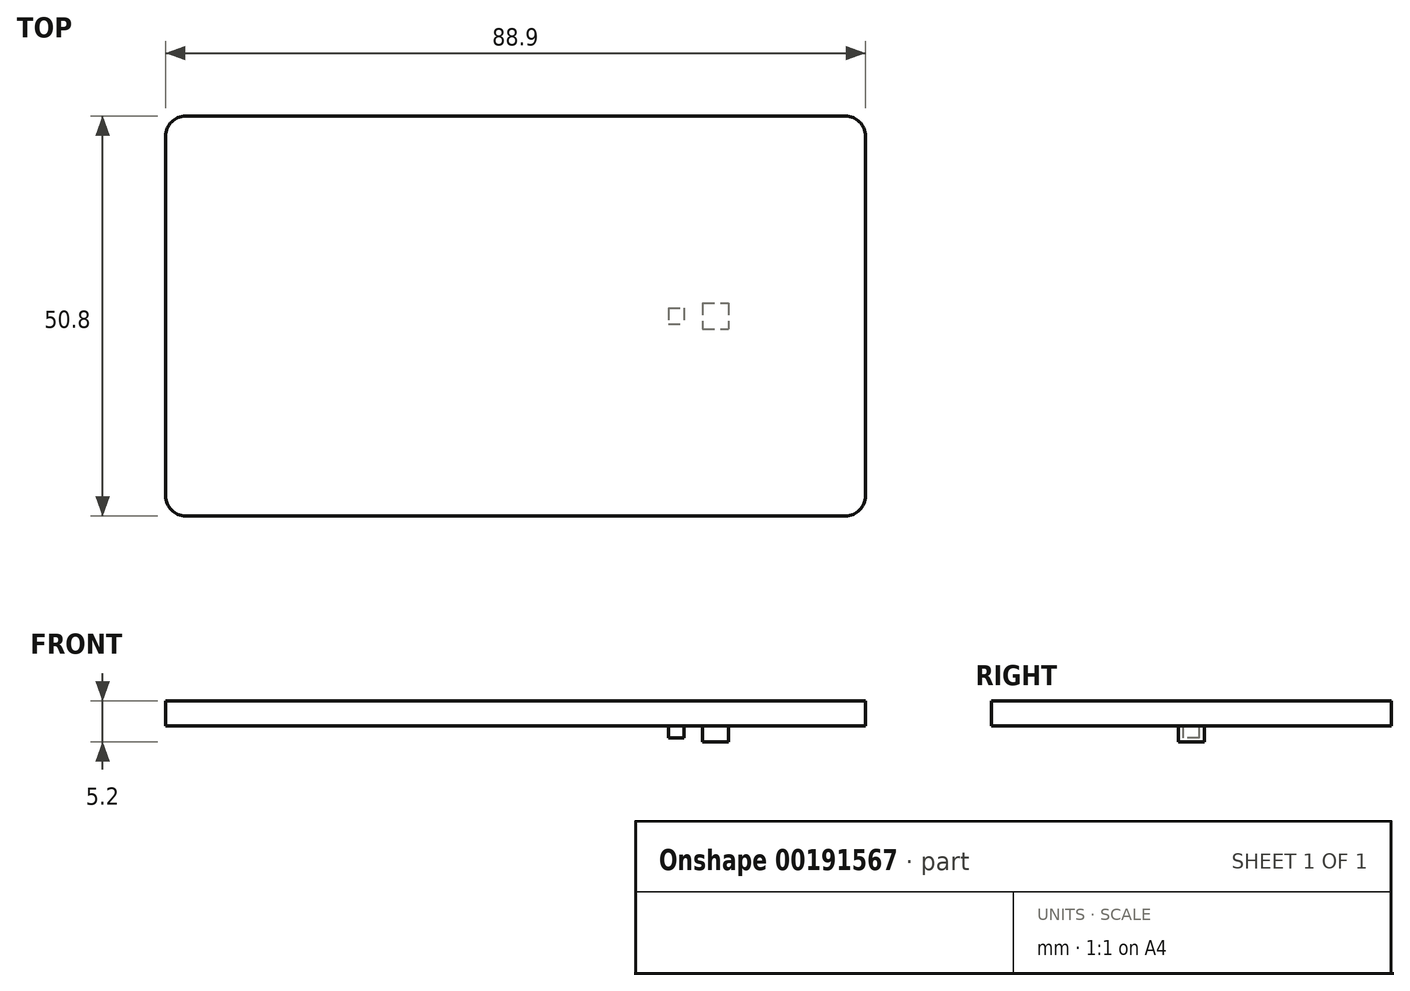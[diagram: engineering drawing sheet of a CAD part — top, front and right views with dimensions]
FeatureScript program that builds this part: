
annotation { "Feature Type Name" : "Feature", "Feature Type Description" : "" }
export const myFeature = defineFeature(function(context is Context, id is Id, definition is map)
    precondition{}
    {
        {
            var Q0;
            Q0=qCreatedBy(makeId("Top.planeOp"),FACE);
            var sketch = newSketch(context, id + "F0", { "sketchPlane" : qUnion([Q0])});
            skLineSegment(sketch, "E0.bottom", {"start": v(44.45, 25.4) * mm, "end": v(-44.45, 25.4) * mm});
            skLineSegment(sketch, "E0.top", {"start": v(44.45, -25.4) * mm, "end": v(-44.45, -25.4) * mm});
            skLineSegment(sketch, "E0.left", {"start": v(44.45, 25.4) * mm, "end": v(44.45, -25.4) * mm});
            skLineSegment(sketch, "E0.right", {"start": v(-44.45, 25.4) * mm, "end": v(-44.45, -25.4) * mm});
            skPoint(sketch, "E0.middle", {"position": v(0, 0) * mm});
            skSolve(sketch);
        }
        {
            var Q0;
            Q0 = qSketchRegion(id + "F0", true);
            extrude(context, id + "F1", {"entities" : qUnion([Q0]), "depth" : 3.2 * mm});
        }
        {
            var Q0;
            Q0=makeQuery(id+"F1.opExtrude","SWEPT_EDGE",EDGE,{"disambiguationData":[OSD([sQuery(id+"F0.wireOp",EDGE,"E0.top"),sQuery(id+"F0.wireOp",EDGE,"E0.left")])]});
            var Q1;
            Q1=makeQuery(id+"F1.opExtrude","SWEPT_EDGE",EDGE,{"disambiguationData":[OSD([sQuery(id+"F0.wireOp",EDGE,"E0.bottom"),sQuery(id+"F0.wireOp",EDGE,"E0.left")])]});
            var Q2;
            Q2=makeQuery(id+"F1.opExtrude","SWEPT_EDGE",EDGE,{"disambiguationData":[OSD([sQuery(id+"F0.wireOp",EDGE,"E0.top"),sQuery(id+"F0.wireOp",EDGE,"E0.right")])]});
            var Q3;
            Q3=makeQuery(id+"F1.opExtrude","SWEPT_EDGE",EDGE,{"disambiguationData":[OSD([sQuery(id+"F0.wireOp",EDGE,"E0.bottom"),sQuery(id+"F0.wireOp",EDGE,"E0.right")])]});
            fillet(context, id + "F2", {"entities" : qUnion([Q0, Q1, Q2, Q3]), "radius" : 2.54 * mm, "tangentPropagation" : true, "allowEdgeOverflow" : false});
        }
        {
            var Q0;
            Q0=makeQuery(id+"F1.opExtrude","CAP_FACE",FACE,{"disambiguationData":[OSD([sQuery(id+"F0.wireOp",EDGE,"E0.bottom"),sQuery(id+"F0.wireOp",EDGE,"E0.top"),sQuery(id+"F0.wireOp",EDGE,"E0.left"),sQuery(id+"F0.wireOp",EDGE,"E0.right")])],"isStart":true});
            var sketch = newSketch(context, id + "F3", { "sketchPlane" : qUnion([Q0])});
            skPoint(sketch, "E1", {"position": v(25.4, 0) * mm});
            skSolve(sketch);
        }
        {
            var Q0;
            {var subQ3=sQuery(id+"F0.wireOp",EDGE,"E0.bottom");Q0=makeQuery(id+"F3.imprint","IMPRINT",FACE,{"disambiguationData":[TD([[makeQuery(id+"F3.imprint","IMPRINT",EDGE,{"derivedFrom":makeQuery(id+"F1.opExtrude","CAP_EDGE",EDGE,{"disambiguationData":[OSD([subQ3])],"isStart":true})}),-1.0]])]});}
            var sketch = newSketch(context, id + "F4", { "sketchPlane" : qUnion([Q0])});
            skLineSegment(sketch, "E2.bottom", {"start": v(23.75, -1.65) * mm, "end": v(27.05, -1.65) * mm});
            skLineSegment(sketch, "E2.top", {"start": v(23.75, 1.65) * mm, "end": v(27.05, 1.65) * mm});
            skLineSegment(sketch, "E2.left", {"start": v(23.75, -1.65) * mm, "end": v(23.75, 1.65) * mm});
            skLineSegment(sketch, "E2.right", {"start": v(27.05, -1.65) * mm, "end": v(27.05, 1.65) * mm});
            skPoint(sketch, "E2.middle", {"position": v(25.4, 0) * mm});
            skSolve(sketch);
        }
        {
            var Q0;
            Q0 = qSketchRegion(id + "F4", true);
            extrude(context, id + "F5", {"entities" : qUnion([Q0]), "operationType" : NewBodyOperationType.ADD, "depth" : 2 * mm});
        }
        {
            var Q0;
            {var subQ3=sQuery(id+"F0.wireOp",EDGE,"E0.bottom");Q0=makeQuery(id+"F3.imprint","IMPRINT",FACE,{"disambiguationData":[TD([[makeQuery(id+"F3.imprint","IMPRINT",EDGE,{"derivedFrom":makeQuery(id+"F1.opExtrude","CAP_EDGE",EDGE,{"disambiguationData":[OSD([subQ3])],"isStart":true})}),-1.0]])]});}
            var sketch = newSketch(context, id + "F6", { "sketchPlane" : qUnion([Q0])});
            skPoint(sketch, "E3", {"position": v(20.4, 0) * mm});
            skSolve(sketch);
        }
        {
            var Q0;
            {var subQ3=sQuery(id+"F0.wireOp",EDGE,"E0.bottom");Q0=makeQuery(id+"F3.imprint","IMPRINT",FACE,{"disambiguationData":[TD([[makeQuery(id+"F3.imprint","IMPRINT",EDGE,{"derivedFrom":makeQuery(id+"F1.opExtrude","CAP_EDGE",EDGE,{"disambiguationData":[OSD([subQ3])],"isStart":true})}),-1.0]])]});}
            var sketch = newSketch(context, id + "F7", { "sketchPlane" : qUnion([Q0])});
            skLineSegment(sketch, "E4.bottom", {"start": v(19.4, -1) * mm, "end": v(21.4, -1) * mm});
            skLineSegment(sketch, "E4.top", {"start": v(19.4, 1) * mm, "end": v(21.4, 1) * mm});
            skLineSegment(sketch, "E4.left", {"start": v(19.4, -1) * mm, "end": v(19.4, 1) * mm});
            skLineSegment(sketch, "E4.right", {"start": v(21.4, -1) * mm, "end": v(21.4, 1) * mm});
            skPoint(sketch, "E4.middle", {"position": v(20.4, 0) * mm});
            skSolve(sketch);
        }
        {
            var Q0;
            Q0 = qSketchRegion(id + "F7", true);
            extrude(context, id + "F8", {"entities" : qUnion([Q0]), "operationType" : NewBodyOperationType.ADD, "depth" : 1.5 * mm});
        }
    });
